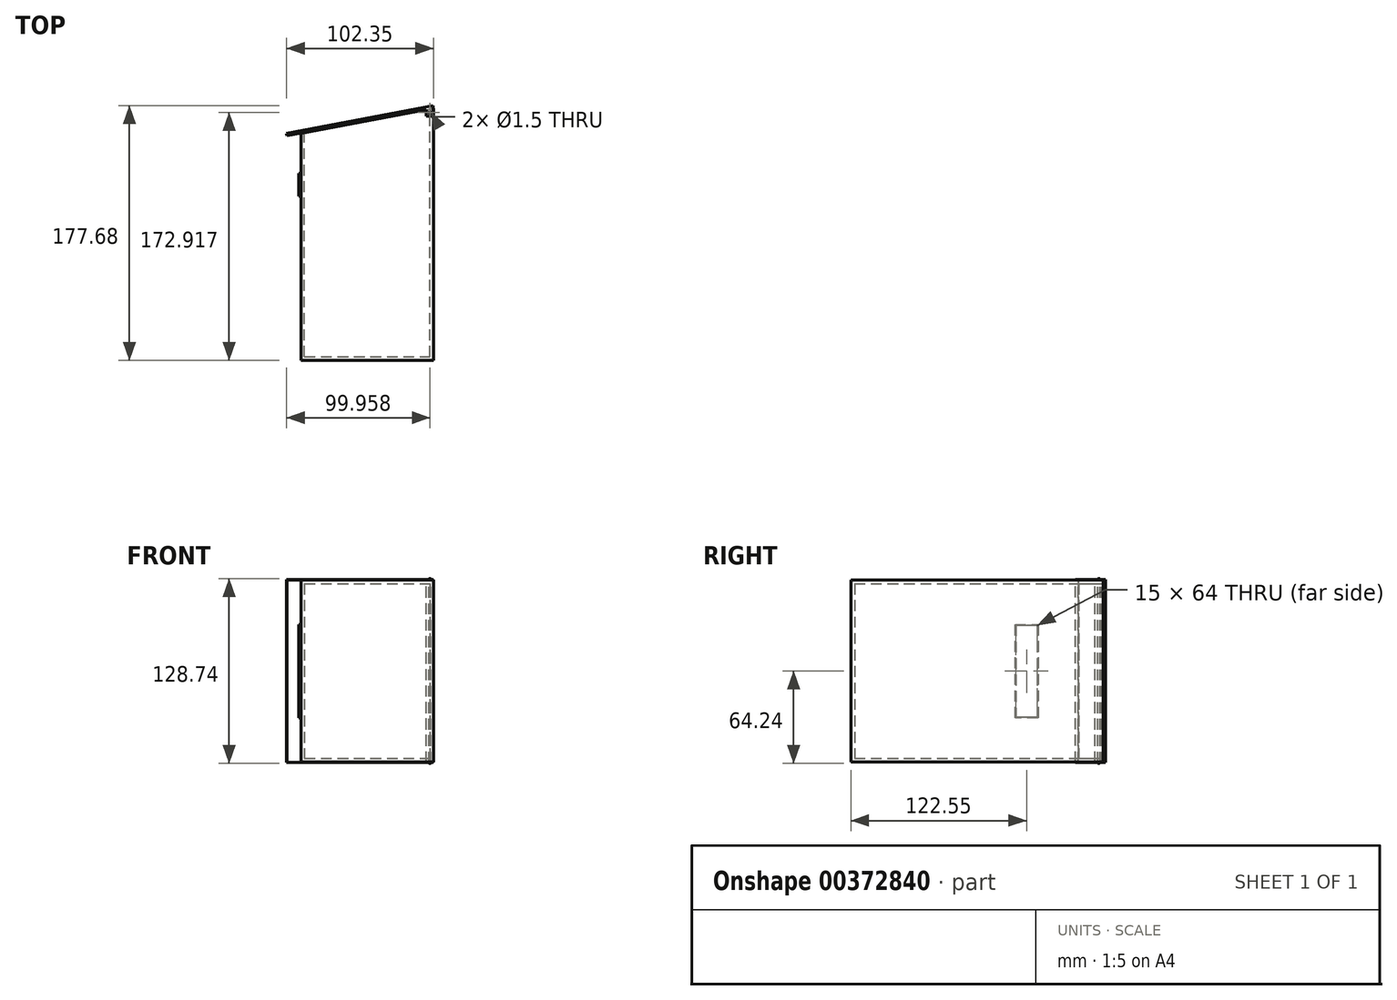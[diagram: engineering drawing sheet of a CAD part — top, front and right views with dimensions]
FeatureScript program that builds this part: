
annotation { "Feature Type Name" : "Feature", "Feature Type Description" : "" }
export const myFeature = defineFeature(function(context is Context, id is Id, definition is map)
    precondition{}
    {
        {
            var Q0;
            Q0=qCreatedBy(makeId("Top.planeOp"),FACE);
            var sketch = newSketch(context, id + "F0", { "sketchPlane" : qUnion([Q0])});
            skLineSegment(sketch, "E0.bottom", {"start": v(-41.44, -115.05) * mm, "end": v(50.93, -115.05) * mm});
            skLineSegment(sketch, "E0.left", {"start": v(-41.44, -115.05) * mm, "end": v(-41.44, 43.44) * mm});
            skLineSegment(sketch, "E0.right", {"start": v(50.93, -115.05) * mm, "end": v(50.93, 60.77) * mm});
            skLineSegment(sketch, "E1", {"start": v(-41.44, 43.44) * mm, "end": v(50.93, 60.77) * mm});
            skSolve(sketch);
        }
        {
            var Q0;
            Q0=makeQuery(id+"F0.imprint","IMPRINT",FACE,{"disambiguationData":[TD([[makeQuery(id+"F0.imprint","IMPRINT",EDGE,{"derivedFrom":sQuery(id+"F0.wireOp",EDGE,"E0.bottom")}),1.0]])]});
            extrude(context, id + "F1", {"entities" : qUnion([Q0]), "depth" : 127 * mm});
        }
        {
            var Q0;
            Q0=makeQuery(id+"F1.opExtrude","SWEPT_FACE",FACE,{"disambiguationData":[OSD([sQuery(id+"F0.wireOp",EDGE,"E1")])]});
            shell(context, id + "F2", {"entities" : qUnion([Q0]), "thickness" : 2.5 * mm});
        }
        {
            var Q0;
            Q0=makeQuery(id+"F1.opExtrude","CAP_FACE",FACE,{"disambiguationData":[OSD([sQuery(id+"F0.wireOp",EDGE,"E0.bottom"),sQuery(id+"F0.wireOp",EDGE,"E0.left"),sQuery(id+"F0.wireOp",EDGE,"E0.right"),sQuery(id+"F0.wireOp",EDGE,"E1")])],"isStart":false});
            var sketch = newSketch(context, id + "F3", { "sketchPlane" : qUnion([Q0])});
            skLineSegment(sketch, "E2", {"start": v(46.15, 59.87) * mm, "end": v(-51.08, 41.63) * mm});
            skLineSegment(sketch, "E3", {"start": v(-51.08, 41.63) * mm, "end": v(-51.42, 43.44) * mm});
            skLineSegment(sketch, "E4", {"start": v(-51.42, 43.44) * mm, "end": v(50.93, 62.64) * mm});
            skLineSegment(sketch, "E5", {"start": v(46.15, 59.87) * mm, "end": v(46.15, 55.29) * mm});
            skLineSegment(sketch, "E6", {"start": v(46.15, 55.29) * mm, "end": v(50.93, 55.29) * mm});
            skCircle(sketch, "E7", {"center": v(48.54, 57.87) * mm, "radius": 0.75 * mm});
            skPoint(sketch, "E7.centerSnap0", {"position": v(48.54, 55.29) * mm});
            skLineSegment(sketch, "E8", {"start": v(50.88, 55.29) * mm, "end": v(50.88, 62.63) * mm});
            skPoint(sketch, "E9.orphan", {"position": v(50.88, 62.64) * mm});
            skSolve(sketch);
        }
        {
            var Q0;
            {var subQ1=sQuery(id+"F3.wireOp",EDGE,"E5");Q0=makeQuery(id+"F3.imprint","IMPRINT",FACE,{"disambiguationData":[TD([[makeQuery(id+"F3.imprint","IMPRINT",EDGE,{"derivedFrom":subQ1}),1.0]])]});}
            var Q1;
            {var subQ0=sQuery(id+"F3.wireOp",EDGE,"E3");Q1=makeQuery(id+"F3.imprint","IMPRINT",FACE,{"disambiguationData":[TD([[makeQuery(id+"F3.imprint","IMPRINT",EDGE,{"derivedFrom":subQ0}),-1.0]])]});}
            extrude(context, id + "F4", {"entities" : qUnion([Q0, Q1]), "oppositeDirection" : true, "depth" : 127.3 * mm});
        }
        {
            var Q0;
            {var subQ0=sQuery(id+"F3.wireOp",EDGE,"E3");Q0=makeQuery(id+"F3.imprint","IMPRINT",FACE,{"disambiguationData":[TD([[makeQuery(id+"F3.imprint","IMPRINT",EDGE,{"derivedFrom":subQ0}),-1.0]])]});}
            var Q1;
            {var subQ1=sQuery(id+"F3.wireOp",EDGE,"E5");Q1=makeQuery(id+"F3.imprint","IMPRINT",FACE,{"disambiguationData":[TD([[makeQuery(id+"F3.imprint","IMPRINT",EDGE,{"derivedFrom":subQ1}),1.0]])]});}
            extrude(context, id + "F5", {"entities" : qUnion([Q0, Q1]), "depth" : 0.4 * mm});
        }
        {
            var Q0;
            Q0=makeQuery(id+"F3.imprint","IMPRINT",FACE,{"disambiguationData":[TD([[makeQuery(id+"F3.imprint","IMPRINT",EDGE,{"derivedFrom":sQuery(id+"F3.wireOp",EDGE,"E7")}),1.0]])]});
            extrude(context, id + "F6", {"entities" : qUnion([Q0]), "depth" : 1 * mm});
        }
        {
            var Q0;
            Q0=makeQuery(id+"F3.imprint","IMPRINT",FACE,{"disambiguationData":[TD([[makeQuery(id+"F3.imprint","IMPRINT",EDGE,{"derivedFrom":sQuery(id+"F3.wireOp",EDGE,"E7")}),1.0]])]});
            extrude(context, id + "F7", {"entities" : qUnion([Q0]), "oppositeDirection" : true, "depth" : 127.74 * mm});
        }
        {
            var Q0;
            Q0=makeQuery(id+"F7.opExtrude","CAP_EDGE",EDGE,{"disambiguationData":[OSD([sQuery(id+"F3.wireOp",EDGE,"E7")])],"isStart":false});
            fillet(context, id + "F8", {"entities" : qUnion([Q0]), "radius" : 0.27 * mm, "tangentPropagation" : true, "allowEdgeOverflow" : false});
        }
        {
            var Q0;
            Q0=makeQuery(id+"F6.opExtrude","CAP_EDGE",EDGE,{"disambiguationData":[OSD([sQuery(id+"F3.wireOp",EDGE,"E7")])],"isStart":false});
            fillet(context, id + "F9", {"entities" : qUnion([Q0]), "radius" : 0.27 * mm, "tangentPropagation" : true, "allowEdgeOverflow" : false});
        }
        {
            var Q0;
            Q0=makeQuery(id+"F1.opExtrude","SWEPT_FACE",FACE,{"disambiguationData":[OSD([sQuery(id+"F0.wireOp",EDGE,"E0.left")])]});
            var sketch = newSketch(context, id + "F10", { "sketchPlane" : qUnion([Q0])});
            skLineSegment(sketch, "E10", {"start": v(-15, 63.5) * mm, "end": v(-15, 31.5) * mm});
            skPoint(sketch, "E10.startSnap0", {"position": v(-43.44, 63.5) * mm});
            skLineSegment(sketch, "E11", {"start": v(-15, 31.5) * mm, "end": v(-15, 95.5) * mm});
            skLineSegment(sketch, "E12", {"start": v(-15, 95.5) * mm, "end": v(0, 95.5) * mm});
            skLineSegment(sketch, "E13", {"start": v(0, 95.5) * mm, "end": v(0, 31.5) * mm});
            skLineSegment(sketch, "E14", {"start": v(0, 31.5) * mm, "end": v(-15, 31.5) * mm});
            skLineSegment(sketch, "E15", {"start": v(-15, 30.96) * mm, "end": v(0.5, 30.96) * mm});
            skLineSegment(sketch, "E16", {"start": v(0.5, 30.96) * mm, "end": v(0.5, 96) * mm});
            skLineSegment(sketch, "E17", {"start": v(0.5, 96) * mm, "end": v(-15.4, 96) * mm});
            skLineSegment(sketch, "E18", {"start": v(-15.4, 96) * mm, "end": v(-15.4, 30.96) * mm});
            skLineSegment(sketch, "E19", {"start": v(-15.4, 30.96) * mm, "end": v(-15, 30.96) * mm});
            skSolve(sketch);
        }
        {
            var Q0;
            {var subQ0=sQuery(id+"F10.wireOp",EDGE,"E12");Q0=makeQuery(id+"F10.imprint","IMPRINT",FACE,{"disambiguationData":[TD([[makeQuery(id+"F10.imprint","IMPRINT",EDGE,{"derivedFrom":subQ0}),-1.0]])]});}
            extrude(context, id + "F11", {"entities" : qUnion([Q0]), "depth" : 1.3 * mm});
        }
        {
            var Q0;
            {var subQ0=sQuery(id+"F10.wireOp",EDGE,"E12");Q0=makeQuery(id+"F10.imprint","IMPRINT",FACE,{"disambiguationData":[TD([[makeQuery(id+"F10.imprint","IMPRINT",EDGE,{"derivedFrom":subQ0}),1.0]])]});}
            extrude(context, id + "F12", {"entities" : qUnion([Q0]), "depth" : 1.6 * mm});
        }
    });
